AUTODESK INVENTOR PART (.ipt)
format: ipt  version: 2017 (Build 210142000, 142)  size: 133,120 bytes
history: native  units: mm
features: extrude x6, sketch x6, plane x1
ambient origin geometry x8: Origin, YZ Plane, XZ Plane, XY Plane, X Axis, Y Axis, Z Axis, Center Point
bodies: Solid1 (feature_tree)
feature tree (13):
  extrude  "Extrusion1"  Depth=30.0mm TaperAngle=0.0deg
  extrude  "Extrusion4"  Depth=5.0mm TaperAngle=0.0deg
  extrude  "Extrusion2"  Depth=40.0mm
  extrude  "Extrusion3"  Depth=21.3mm
  extrude  "Extrusion5"  Depth=0.5mm TaperAngle=0.0deg
  plane  "Work Plane1"
  extrude  "Extrusion6"  Depth=22.0mm
  sketch  "Sketch1"  dims[d0=100.0mm d1=30.0mm d2=0.0mm]
  sketch  "Sketch2"  dims[d3=5.0mm d4=5.0mm d5=0.0mm]
  sketch  "Sketch3"  dims[d6=8.0mm d7=40.0mm]
  sketch  "Sketch4"  dims[d8=2.0mm d9=0.0mm d10=21.3mm]
  sketch  "Sketch5"  dims[d11=83.5mm d12=0.0mm d13=0.5mm d14=0.0mm]
  sketch  "Sketch7"  dims[d15=-20.0mm d16=22.0mm d17=6.0mm d18=0.0mm d19=-15.0mm]
